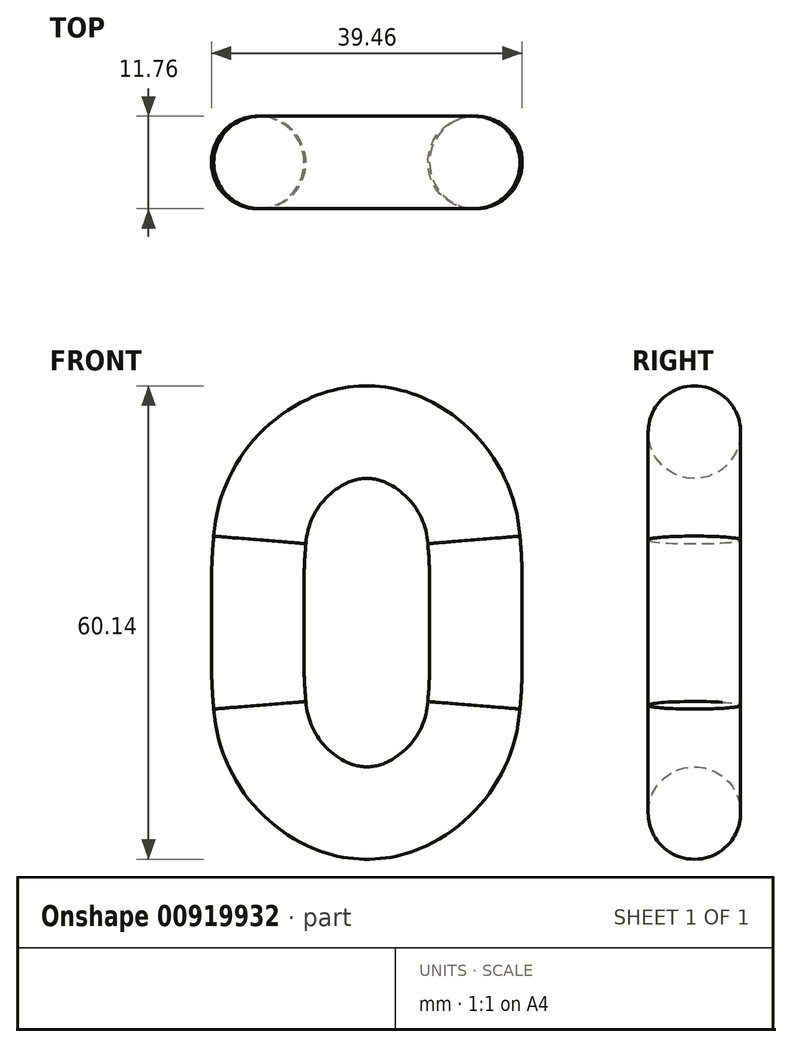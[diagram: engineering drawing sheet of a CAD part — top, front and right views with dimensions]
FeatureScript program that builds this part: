
annotation { "Feature Type Name" : "Feature", "Feature Type Description" : "" }
export const myFeature = defineFeature(function(context is Context, id is Id, definition is map)
    precondition{}
    {
        {
            var Q0;
            Q0=qCreatedBy(makeId("Top.planeOp"),FACE);
            var sketch = newSketch(context, id + "F0", { "sketchPlane" : qUnion([Q0])});
            skPoint(sketch, "E0", {"position": v(13.86, 0) * mm});
            skCircle(sketch, "E1", {"center": v(13.86, 0) * mm, "radius": 5.88 * mm});
            skSolve(sketch);
        }
        {
            var Q0;
            Q0=qCreatedBy(makeId("Front.planeOp"),FACE);
            var sketch = newSketch(context, id + "F1", { "sketchPlane" : qUnion([Q0])});
            skPoint(sketch, "E2", {"position": v(0, 24.2) * mm});
            skPoint(sketch, "E3", {"position": v(13.86, 0) * mm});
            skPoint(sketch, "E4", {"position": v(0, 12.44) * mm});
            skLineSegment(sketch, "E5", {"start": v(13.86, 0) * mm, "end": v(13.86, 5) * mm});
            skArc(sketch, "E6", {"start": v(0, 24.2) * mm, "mid": v(2.58, 23.9) * mm, "end": v(5.04, 23.05) * mm});
            skPoint(sketch, "E7", {"position": v(-44.9, 5) * mm});
            skLineSegment(sketch, "E8", {"start": v(-1.57, 9.14) * mm, "end": v(-1.26, 9.79) * mm});
            skPoint(sketch, "E9", {"position": v(-1.41, 9.46) * mm});
            skArc(sketch, "E10", {"start": v(13.85, 5) * mm, "mid": v(13.8, 7.75) * mm, "end": v(13.6, 10.5) * mm});
            skArc(sketch, "E11", {"start": v(5.04, 23.05) * mm, "mid": v(11.02, 17.94) * mm, "end": v(13.6, 10.5) * mm});
            skLineSegment(sketch, "E12.MirrorCS", {"start": v(-13.86, 0) * mm, "end": v(-13.86, 5) * mm});
            skLineSegment(sketch, "E13.MirrorCS", {"start": v(1.57, 9.14) * mm, "end": v(1.26, 9.79) * mm});
            skArc(sketch, "E14.MirrorCS", {"start": v(0, 24.2) * mm, "mid": v(-2.58, 23.9) * mm, "end": v(-5.04, 23.05) * mm});
            skArc(sketch, "E15.MirrorCS", {"start": v(-13.85, 5) * mm, "mid": v(-13.8, 7.75) * mm, "end": v(-13.6, 10.5) * mm});
            skPoint(sketch, "E16.MirrorP", {"position": v(1.41, 9.46) * mm});
            skPoint(sketch, "E17.MirrorP", {"position": v(-13.86, 0) * mm});
            skArc(sketch, "E18.MirrorCS", {"start": v(-5.04, 23.05) * mm, "mid": v(-11.02, 17.94) * mm, "end": v(-13.6, 10.5) * mm});
            skLineSegment(sketch, "E19.MirrorCS", {"start": v(1.57, -9.14) * mm, "end": v(1.26, -9.79) * mm});
            skLineSegment(sketch, "E20.MirrorCS", {"start": v(-1.57, -9.14) * mm, "end": v(-1.26, -9.79) * mm});
            skPoint(sketch, "E21.MirrorP", {"position": v(0, -24.2) * mm});
            skPoint(sketch, "E22.MirrorP", {"position": v(0, -12.44) * mm});
            skArc(sketch, "E23.MirrorCS", {"start": v(-5.04, -23.05) * mm, "mid": v(-11.02, -17.94) * mm, "end": v(-13.6, -10.5) * mm});
            skArc(sketch, "E24.MirrorCS", {"start": v(0, -24.2) * mm, "mid": v(2.58, -23.9) * mm, "end": v(5.04, -23.05) * mm});
            skArc(sketch, "E25.MirrorCS", {"start": v(5.04, -23.05) * mm, "mid": v(11.02, -17.94) * mm, "end": v(13.6, -10.5) * mm});
            skArc(sketch, "E26.MirrorCS", {"start": v(-13.85, -5) * mm, "mid": v(-13.8, -7.75) * mm, "end": v(-13.6, -10.5) * mm});
            skArc(sketch, "E27.MirrorCS", {"start": v(0, -24.2) * mm, "mid": v(-2.58, -23.9) * mm, "end": v(-5.04, -23.05) * mm});
            skLineSegment(sketch, "E28.MirrorCS", {"start": v(13.86, 0) * mm, "end": v(13.86, -5) * mm});
            skLineSegment(sketch, "E29.MirrorCS", {"start": v(-13.86, 0) * mm, "end": v(-13.86, -5) * mm});
            skArc(sketch, "E30.MirrorCS", {"start": v(13.85, -5) * mm, "mid": v(13.8, -7.75) * mm, "end": v(13.6, -10.5) * mm});
            skSolve(sketch);
        }
        {
            var Q0;
            Q0=makeQuery(id+"F0.imprint","IMPRINT",FACE,{"disambiguationData":[TD([[makeQuery(id+"F0.imprint","IMPRINT",EDGE,{"derivedFrom":sQuery(id+"F0.wireOp",EDGE,"E1")}),1.0]])]});
            var Q1;
            Q1=sQuery(id+"F1.wireOp",EDGE,"E5");
            var Q2;
            Q2=sQuery(id+"F1.wireOp",EDGE,"E10");
            var Q3;
            Q3=sQuery(id+"F1.wireOp",EDGE,"E11");
            var Q4;
            Q4=sQuery(id+"F1.wireOp",EDGE,"E6");
            var Q5;
            Q5=sQuery(id+"F1.wireOp",EDGE,"E14.MirrorCS");
            var Q6;
            Q6=sQuery(id+"F1.wireOp",EDGE,"E18.MirrorCS");
            var Q7;
            Q7=sQuery(id+"F1.wireOp",EDGE,"E15.MirrorCS");
            var Q8;
            Q8=sQuery(id+"F1.wireOp",EDGE,"E12.MirrorCS");
            var Q9;
            Q9=sQuery(id+"F1.wireOp",EDGE,"E29.MirrorCS");
            var Q10;
            Q10=sQuery(id+"F1.wireOp",EDGE,"E26.MirrorCS");
            var Q11;
            Q11=sQuery(id+"F1.wireOp",EDGE,"E23.MirrorCS");
            var Q12;
            Q12=sQuery(id+"F1.wireOp",EDGE,"E27.MirrorCS");
            var Q13;
            Q13=sQuery(id+"F1.wireOp",EDGE,"E24.MirrorCS");
            var Q14;
            Q14=sQuery(id+"F1.wireOp",EDGE,"E25.MirrorCS");
            var Q15;
            Q15=sQuery(id+"F1.wireOp",EDGE,"E30.MirrorCS");
            var Q16;
            Q16=sQuery(id+"F1.wireOp",EDGE,"E28.MirrorCS");
            sweep(context, id + "F2", {"profiles" : qUnion([Q0]), "path" : qUnion([Q1, Q2, Q3, Q4, Q5, Q6, Q7, Q8, Q9, Q10, Q11, Q12, Q13, Q14, Q15, Q16])});
        }
    });
